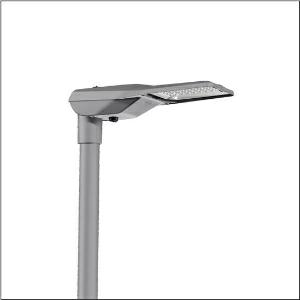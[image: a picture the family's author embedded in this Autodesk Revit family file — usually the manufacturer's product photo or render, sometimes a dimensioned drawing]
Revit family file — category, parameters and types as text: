
# Revit family: streetlight_sl_21_iq_mini___st1_0a_5xe2d61y08hb_d678
name_source: partatom
category: Lighting Fixtures
units: mm (PartAtom-declared; Revit-internal decimal feet)

## family parameters
Cut with Voids When Loaded = No
Host = Face
Light Source = No
Part Type = Normal
Room Calculation Point = No
Round Connector Dimension = Use Diameter
Shared = No

## types (1)
- --- (1 x LED, 8460 lm, 71 W, 2700K)
    Apparent Load = 71 VA
    CIE Flux Codes = 37 72 97 100 100
    Color Rendering = 70
    Color Temperature = 2700K
    Default Elevation = 1800 mm
    Description = Streetlight SL 21 iQ mini, mast luminaire, primary light control with lens, of PMMA, primary optical cover: cover, of toughened safety glass, transparent, light distribution: ST1.0a, light emission: direct distribution, primary light characteristic: asymmetric, installation type: post-top, side-entry, LED, High Power LED, rated luminous flux: 8.460lm, luminous efficacy: 119lm/W, light colour: 727, colour temperature: 2700K, control: presetting dimming logarithmic, Street-Remote, Auto-Match, Temp-Guard, Lumen-Switch, Night-Set, Smart-Wire, Light-Fading, Desk-Remote (wireless, voltage-free reading and setting of iQ features in the workshop via application-optimized NFC function/RFID function), optimised constant luminous flux control (CLO 2.0), mains connection: 220..240V, AC, 50/60Hz, start of lifetime: 71W, end of service life: 75W, reduction: 30W, luminaire housing, of diecast aluminium, powder-coated, Siteco® metallic grey (DB 702S), corrosivity category C5 mid according to DIN EN ISO 12944, please order mast flange separately, inclination adjustable: 0°, 5°, 10°, 15°, sealing non-destructively replaceable, multi-level sealing system, length: 628mm, width: 235mm, height: 110mm, mast flange for spigot size: 42mm (side-entry): 5XC10008XM4, 60/48mm (side-entry/post-top): 5XC10108XM2, 76/60mm (side-entry/post-top): 5XC10108XM1, Smart Interface below and above, protection rating (complete): IP66, insulation class (complete): insulation class II (safety insulation), certification: CE, ENEC, ENEC+, VDE, impact resistance: IK09, permissible operating ambient temperature for outdoor applications: -40..+50°C, standard-compliant lighting for roads and squares, packaging unit: 1 piece

Light Distribution: ST1.0a
    Height = 110 mm
    Lamp = 1 x LED
    Lamp Light Flux = 8460 lm
    Lamp Power = 71 W
    Lamp count = 1
    Length = 625 mm
    Luminous efficacy = 119 lm/W
    Manufacturer = Siteco
    ModVariant = No
    Model = 5XE2D61Y08HB
    Number of Poles = 1
    OnlyDefault = Yes
    Power Factor = 1
    Product Name = Streetlight SL 21 iQ mini | ST1.0a
    Product group = mast luminaire | pylon top
    ProductGroupID = 6100
    Protection Class = Protection class II
    Protection Degree = IP 66
    RLX_Detail_Level = 1
    RLX_Emergency_Light_Flux = 0 lm
    RLX_Emergency_Type = 0
    RLX_Emergency_Type_DB = No
    RlxData = <blob elided: 92289 chars, md5=c5718f49>
    Socket = socket
    Standby Power = 0 W
    System Light Flux = 8460 lm
    System Power = 71 W
    Type Comments = factory setting: luminous flux: 100 % | dim-lin: 254 | 716 mA
    Type Image = l_1003514.jpg
    URL = http://relux.com
    VarID = @adj_044993
    Voltage = 0 V
    Weight = 0.00 kg
    Width = 234 mm

## geometry (parser evidence)
native form markers: Blend x4, Sweep x11
no freeform markers — native parametric forms only
